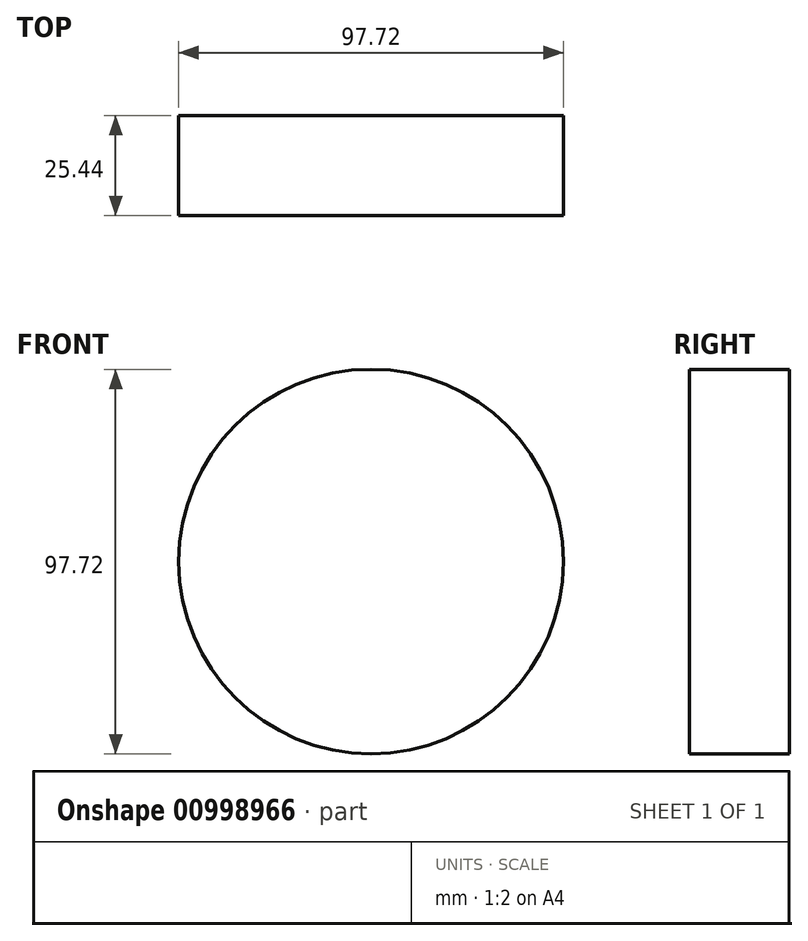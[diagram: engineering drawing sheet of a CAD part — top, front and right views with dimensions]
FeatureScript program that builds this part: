
annotation { "Feature Type Name" : "Feature", "Feature Type Description" : "" }
export const myFeature = defineFeature(function(context is Context, id is Id, definition is map)
    precondition{}
    {
        {
            var Q0;
            Q0=qCreatedBy(makeId("Front.planeOp"),FACE);
            var sketch = newSketch(context, id + "F0", { "sketchPlane" : qUnion([Q0])});
            skCircle(sketch, "E0", {"center": v(0, 0) * mm, "radius": 48.86 * mm});
            skSolve(sketch);
        }
        {
            var Q0;
            Q0=makeQuery(id+"F0.imprint","IMPRINT",FACE,{"disambiguationData":[TD([[makeQuery(id+"F0.imprint","IMPRINT",EDGE,{"derivedFrom":sQuery(id+"F0.wireOp",EDGE,"E0")}),1.0]])]});
            var sketch = newSketch(context, id + "F1", { "sketchPlane" : qUnion([Q0])});
            skPoint(sketch, "E1.0", {"position": v(0, 0) * mm});
            skSolve(sketch);
        }
        {
            var Q0;
            Q0=makeQuery(id+"F1.imprint","IMPRINT",FACE,{"disambiguationData":[TD([[makeQuery(id+"F1.imprint","IMPRINT",EDGE,{"derivedFrom":makeQuery(id+"F0.imprint","IMPRINT",EDGE,{"derivedFrom":sQuery(id+"F0.wireOp",EDGE,"E0")})}),1.0]])]});
            extrude(context, id + "F2", {"entities" : qUnion([Q0]), "depth" : 25.44 * mm, "offsetDistance" : 25.4 * mm});
        }
    });
